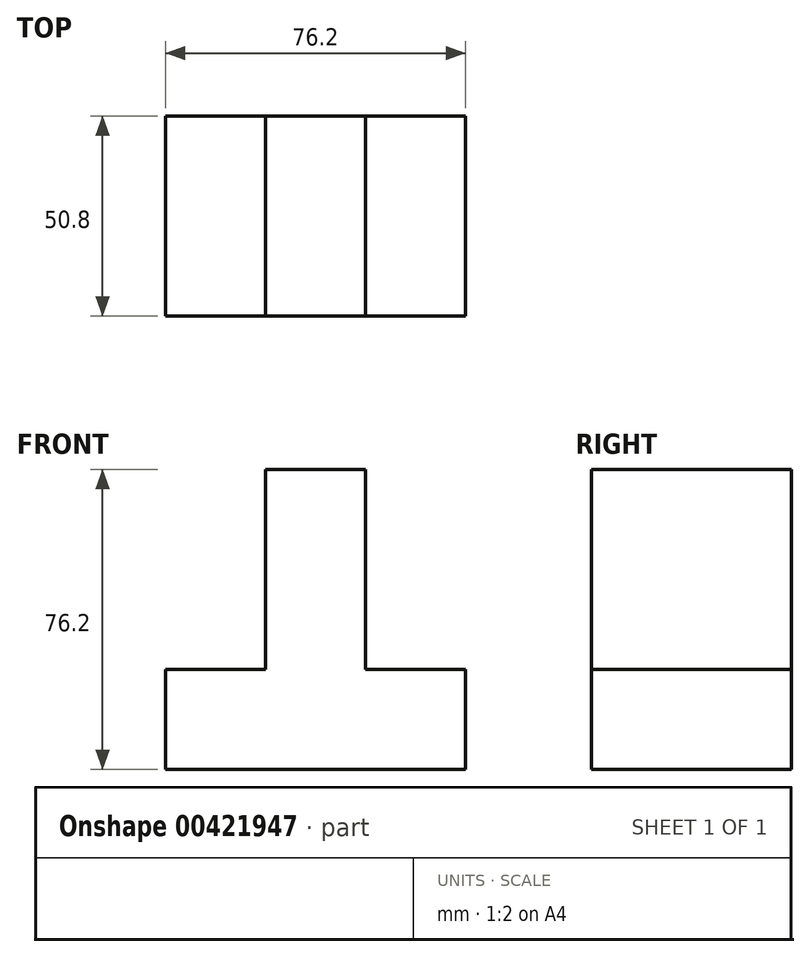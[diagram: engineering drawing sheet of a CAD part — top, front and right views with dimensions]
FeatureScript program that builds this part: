
annotation { "Feature Type Name" : "Feature", "Feature Type Description" : "" }
export const myFeature = defineFeature(function(context is Context, id is Id, definition is map)
    precondition{}
    {
        {
            var Q0;
            Q0=qCreatedBy(makeId("Front.planeOp"),FACE);
            var sketch = newSketch(context, id + "F0", { "sketchPlane" : qUnion([Q0])});
            skLineSegment(sketch, "E0", {"start": v(-76.2, 0) * mm, "end": v(0, 0) * mm});
            skLineSegment(sketch, "E1", {"start": v(-76.2, 0) * mm, "end": v(-76.2, 25.4) * mm});
            skLineSegment(sketch, "E2", {"start": v(0, 0) * mm, "end": v(0, 25.4) * mm});
            skLineSegment(sketch, "E3", {"start": v(-76.2, 25.4) * mm, "end": v(-50.8, 25.4) * mm});
            skLineSegment(sketch, "E4", {"start": v(0, 25.4) * mm, "end": v(-25.4, 25.4) * mm});
            skLineSegment(sketch, "E5", {"start": v(-50.8, 25.4) * mm, "end": v(-50.8, 76.2) * mm});
            skLineSegment(sketch, "E6", {"start": v(-25.4, 25.4) * mm, "end": v(-25.4, 76.2) * mm});
            skLineSegment(sketch, "E7", {"start": v(-50.8, 76.2) * mm, "end": v(-25.4, 76.2) * mm});
            skSolve(sketch);
        }
        {
            var Q0;
            Q0 = qSketchRegion(id + "F0", true);
            extrude(context, id + "F1", {"entities" : qUnion([Q0]), "depth" : 50.8 * mm});
        }
    });
